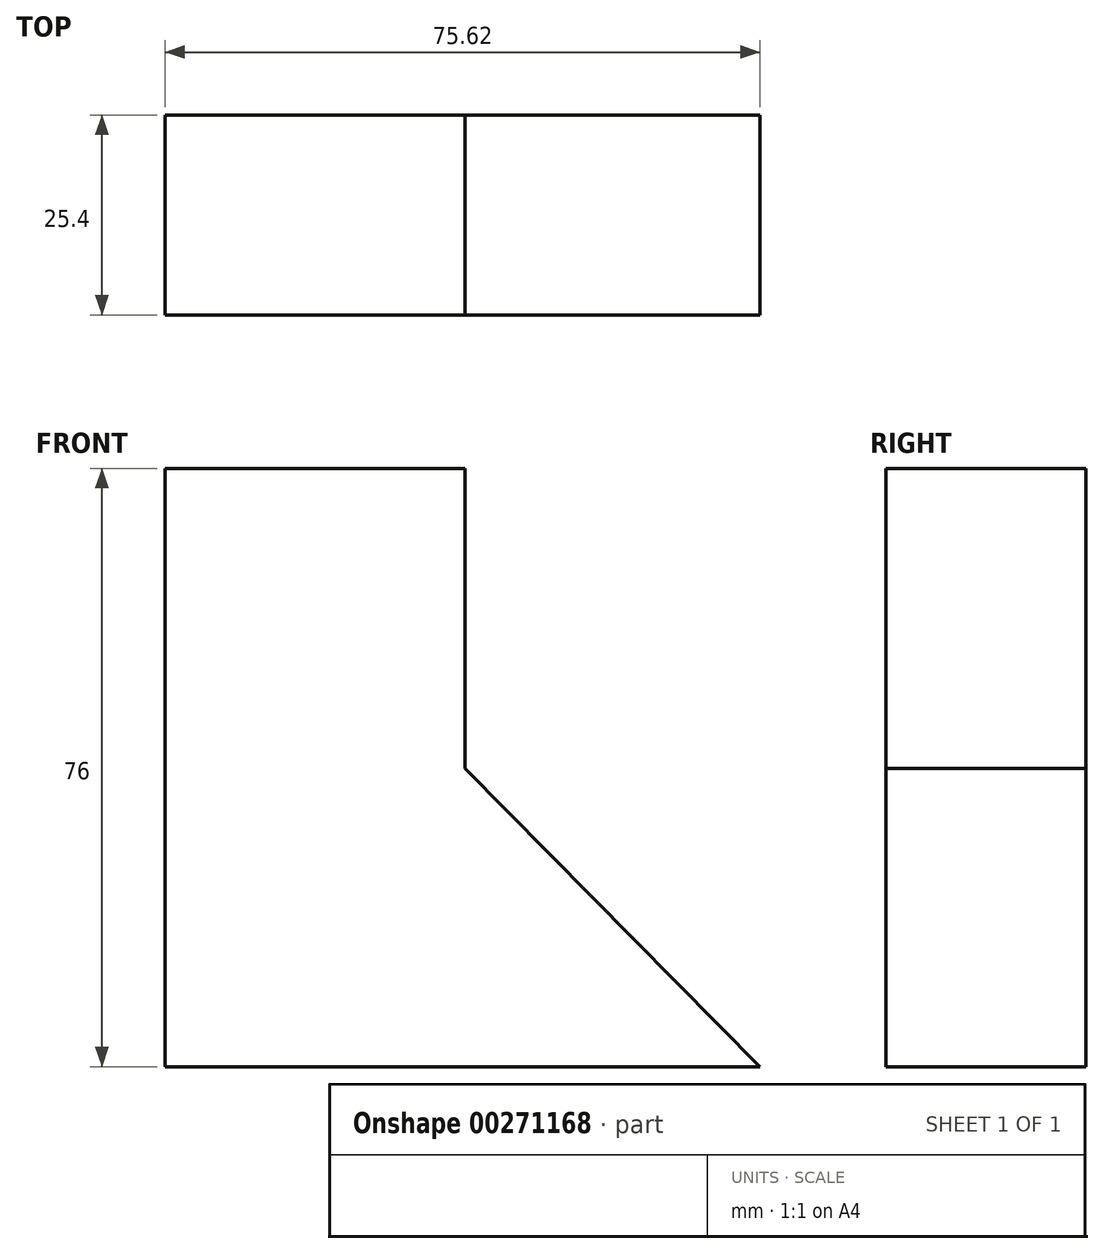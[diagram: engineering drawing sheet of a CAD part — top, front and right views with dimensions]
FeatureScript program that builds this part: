
annotation { "Feature Type Name" : "Feature", "Feature Type Description" : "" }
export const myFeature = defineFeature(function(context is Context, id is Id, definition is map)
    precondition{}
    {
        {
            var Q0;
            Q0=qCreatedBy(makeId("Front.planeOp"),FACE);
            var sketch = newSketch(context, id + "F0", { "sketchPlane" : qUnion([Q0])});
            skLineSegment(sketch, "E0", {"start": v(0, 0) * mm, "end": v(-75.62, 0) * mm});
            skLineSegment(sketch, "E1", {"start": v(-75.62, 0) * mm, "end": v(-75.62, 76) * mm});
            skLineSegment(sketch, "E2", {"start": v(-75.62, 76) * mm, "end": v(-37.52, 76) * mm});
            skLineSegment(sketch, "E3", {"start": v(-37.52, 76) * mm, "end": v(-37.52, 37.9) * mm});
            skLineSegment(sketch, "E4", {"start": v(-37.52, 37.9) * mm, "end": v(0, 0) * mm});
            skSolve(sketch);
        }
        {
            var Q0;
            Q0 = qSketchRegion(id + "F0", true);
            extrude(context, id + "F1", {"entities" : qUnion([Q0]), "depth" : 25.4 * mm});
        }
    });
